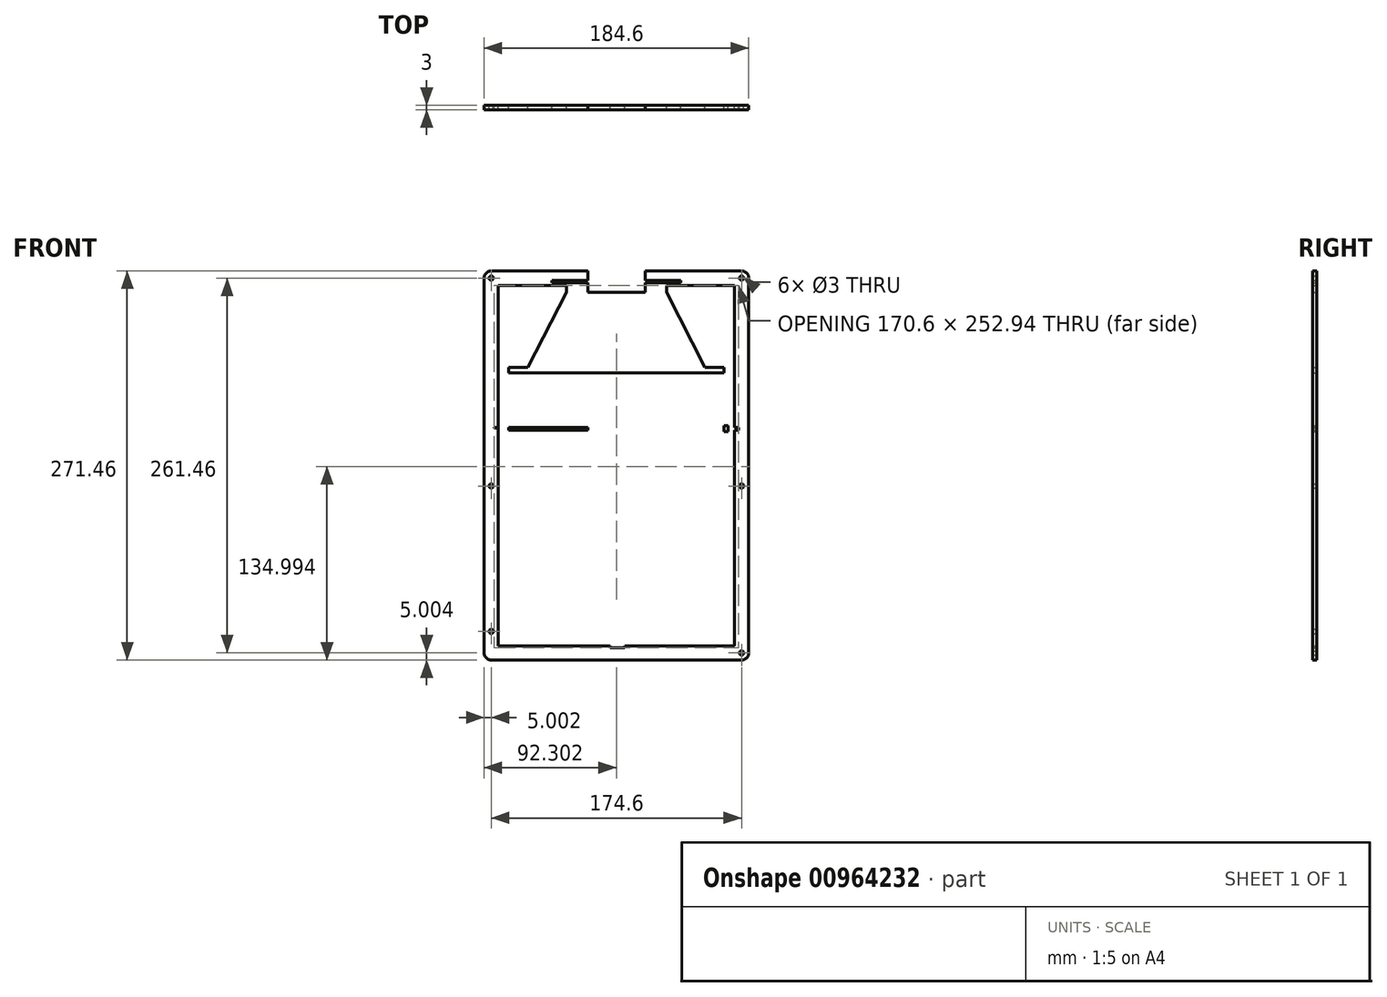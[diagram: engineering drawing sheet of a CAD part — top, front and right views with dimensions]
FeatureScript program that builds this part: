
annotation { "Feature Type Name" : "Feature", "Feature Type Description" : "" }
export const myFeature = defineFeature(function(context is Context, id is Id, definition is map)
    precondition{}
    {
        {
            var Q0;
            Q0=qCreatedBy(makeId("Front.planeOp"),FACE);
            var sketch = newSketch(context, id + "F0", { "sketchPlane" : qUnion([Q0])});
            skLineSegment(sketch, "E0.bottom", {"start": v(-91.77, 132.51) * mm, "end": v(82.83, 132.51) * mm});
            skLineSegment(sketch, "E0.top", {"start": v(-91.77, -138.95) * mm, "end": v(82.83, -138.95) * mm});
            skLineSegment(sketch, "E0.left", {"start": v(-96.77, 127.51) * mm, "end": v(-96.77, -133.95) * mm});
            skLineSegment(sketch, "E0.right", {"start": v(87.83, 127.51) * mm, "end": v(87.83, -133.95) * mm});
            skPoint(sketch, "E1.visualSharp", {"position": v(-96.77, 132.51) * mm});
            skArc(sketch, "E1.filletArc", {"start": v(-91.77, 132.51) * mm, "mid": v(-95.3, 131.05) * mm, "end": v(-96.77, 127.51) * mm});
            skPoint(sketch, "E2.visualSharp", {"position": v(87.83, 132.51) * mm});
            skArc(sketch, "E2.filletArc", {"start": v(87.83, 127.51) * mm, "mid": v(86.37, 131.05) * mm, "end": v(82.83, 132.51) * mm});
            skPoint(sketch, "E3.visualSharp", {"position": v(87.83, -138.95) * mm});
            skArc(sketch, "E3.filletArc", {"start": v(82.83, -138.95) * mm, "mid": v(86.37, -137.48) * mm, "end": v(87.83, -133.95) * mm});
            skPoint(sketch, "E4.visualSharp", {"position": v(-96.77, -138.95) * mm});
            skArc(sketch, "E4.filletArc", {"start": v(-96.77, -133.95) * mm, "mid": v(-95.3, -137.48) * mm, "end": v(-91.77, -138.95) * mm});
            skCircle(sketch, "E5", {"center": v(-91.77, 127.51) * mm, "radius": 1.5 * mm});
            skCircle(sketch, "E6", {"center": v(82.83, 127.51) * mm, "radius": 1.5 * mm});
            skCircle(sketch, "E7", {"center": v(82.83, -133.95) * mm, "radius": 1.5 * mm});
            skCircle(sketch, "E8", {"center": v(-91.77, -17.49) * mm, "radius": 1.5 * mm});
            skCircle(sketch, "E9", {"center": v(82.83, -17.49) * mm, "radius": 1.5 * mm});
            skLineSegment(sketch, "E10.bottom", {"start": v(-86.77, 122.51) * mm, "end": v(77.83, 122.51) * mm});
            skLineSegment(sketch, "E10.top", {"start": v(-86.77, -128.95) * mm, "end": v(77.83, -128.95) * mm});
            skLineSegment(sketch, "E10.left", {"start": v(-86.77, 122.51) * mm, "end": v(-86.77, -128.95) * mm});
            skLineSegment(sketch, "E10.right", {"start": v(77.83, 122.51) * mm, "end": v(77.83, -128.95) * mm});
            skLineSegment(sketch, "E11.bottom", {"start": v(-8.77, -128.95) * mm, "end": v(1.23, -128.95) * mm});
            skLineSegment(sketch, "E11.top", {"start": v(-8.77, -130.43) * mm, "end": v(1.23, -130.43) * mm});
            skLineSegment(sketch, "E11.left", {"start": v(-8.77, -128.95) * mm, "end": v(-8.77, -130.43) * mm});
            skLineSegment(sketch, "E11.right", {"start": v(1.23, -128.95) * mm, "end": v(1.23, -130.43) * mm});
            skLineSegment(sketch, "E12.bottom", {"start": v(-11.27, -130.43) * mm, "end": v(3.73, -130.43) * mm});
            skLineSegment(sketch, "E12.top", {"start": v(-11.27, -132.03) * mm, "end": v(3.73, -132.03) * mm});
            skLineSegment(sketch, "E12.left", {"start": v(-11.27, -130.43) * mm, "end": v(-11.27, -132.03) * mm});
            skLineSegment(sketch, "E12.right", {"start": v(3.73, -130.43) * mm, "end": v(3.73, -132.03) * mm});
            skLineSegment(sketch, "E13.bottom", {"start": v(-89.77, 23.45) * mm, "end": v(80.83, 23.45) * mm});
            skLineSegment(sketch, "E13.top", {"start": v(-89.77, 21.45) * mm, "end": v(80.83, 21.45) * mm});
            skLineSegment(sketch, "E13.left", {"start": v(-89.77, 23.45) * mm, "end": v(-89.77, 21.45) * mm});
            skLineSegment(sketch, "E13.right", {"start": v(80.83, 23.45) * mm, "end": v(80.83, 21.45) * mm});
            skLineSegment(sketch, "E14.bottom", {"start": v(-86.77, 23.45) * mm, "end": v(77.83, 23.45) * mm});
            skLineSegment(sketch, "E14.left", {"start": v(-86.77, 23.45) * mm, "end": v(-86.77, 24.64) * mm});
            skLineSegment(sketch, "E14.right", {"start": v(77.83, 23.45) * mm, "end": v(77.83, 24.64) * mm});
            skLineSegment(sketch, "E15.bottom", {"start": v(77.83, 21.45) * mm, "end": v(-86.77, 21.45) * mm});
            skLineSegment(sketch, "E15.top", {"start": v(77.83, 16.15) * mm, "end": v(-86.77, 16.15) * mm});
            skLineSegment(sketch, "E15.left", {"start": v(77.83, 21.45) * mm, "end": v(77.83, 16.15) * mm});
            skLineSegment(sketch, "E15.right", {"start": v(-86.77, 21.45) * mm, "end": v(-86.77, 16.15) * mm});
            skLineSegment(sketch, "E16.bottom", {"start": v(-39.47, 124.21) * mm, "end": v(30.53, 124.21) * mm});
            skLineSegment(sketch, "E16.top", {"start": v(-39.47, 122.51) * mm, "end": v(30.53, 122.51) * mm});
            skLineSegment(sketch, "E16.left", {"start": v(-39.47, 124.21) * mm, "end": v(-39.47, 122.51) * mm});
            skLineSegment(sketch, "E16.right", {"start": v(30.53, 124.21) * mm, "end": v(30.53, 122.51) * mm});
            skLineSegment(sketch, "E17.bottom", {"start": v(-49.47, 125.81) * mm, "end": v(40.53, 125.81) * mm});
            skLineSegment(sketch, "E17.top", {"start": v(-49.47, 124.21) * mm, "end": v(40.53, 124.21) * mm});
            skLineSegment(sketch, "E17.left", {"start": v(-49.47, 125.81) * mm, "end": v(-49.47, 124.21) * mm});
            skLineSegment(sketch, "E17.right", {"start": v(40.53, 125.81) * mm, "end": v(40.53, 124.21) * mm});
            skLineSegment(sketch, "E18.bottom", {"start": v(-24.47, 132.51) * mm, "end": v(15.53, 132.51) * mm});
            skLineSegment(sketch, "E18.top", {"start": v(-24.47, 125.81) * mm, "end": v(15.53, 125.81) * mm});
            skLineSegment(sketch, "E18.left", {"start": v(-24.47, 132.51) * mm, "end": v(-24.47, 125.81) * mm});
            skLineSegment(sketch, "E18.right", {"start": v(15.53, 132.51) * mm, "end": v(15.53, 125.81) * mm});
            skLineSegment(sketch, "E19.bottom", {"start": v(30.53, 124.21) * mm, "end": v(40.53, 124.21) * mm});
            skLineSegment(sketch, "E19.top", {"start": v(21.23, 125.81) * mm, "end": v(40.53, 125.81) * mm});
            skLineSegment(sketch, "E19.right", {"start": v(40.53, 124.21) * mm, "end": v(40.53, 125.81) * mm});
            skLineSegment(sketch, "E20.bottom", {"start": v(-39.47, 124.21) * mm, "end": v(-49.47, 124.21) * mm});
            skLineSegment(sketch, "E20.top", {"start": v(-28.77, 125.81) * mm, "end": v(-49.47, 125.81) * mm});
            skLineSegment(sketch, "E20.right", {"start": v(-49.47, 124.21) * mm, "end": v(-49.47, 125.81) * mm});
            skLineSegment(sketch, "E21.bottom", {"start": v(30.53, 122.51) * mm, "end": v(40.53, 122.51) * mm});
            skLineSegment(sketch, "E22.bottom", {"start": v(-39.47, 122.51) * mm, "end": v(-40.47, 122.51) * mm});
            skLineSegment(sketch, "E23.top", {"start": v(-86.77, -22.49) * mm, "end": v(-96.77, -22.49) * mm});
            skLineSegment(sketch, "E23.left", {"start": v(-86.77, -130.99) * mm, "end": v(-86.77, -22.49) * mm});
            skLineSegment(sketch, "E23.right", {"start": v(-96.77, -132.28) * mm, "end": v(-96.77, -22.49) * mm});
            skLineSegment(sketch, "E24.top", {"start": v(-39.47, 117.51) * mm, "end": v(30.53, 117.51) * mm});
            skLineSegment(sketch, "E24.left", {"start": v(-39.47, 122.51) * mm, "end": v(-39.47, 117.51) * mm});
            skLineSegment(sketch, "E24.right", {"start": v(30.53, 122.51) * mm, "end": v(30.53, 117.51) * mm});
            skLineSegment(sketch, "E25.bottom", {"start": v(-96.77, -113.95) * mm, "end": v(-86.77, -113.95) * mm});
            skLineSegment(sketch, "E25.top", {"start": v(-96.77, -128.95) * mm, "end": v(-86.77, -128.95) * mm});
            skLineSegment(sketch, "E25.left", {"start": v(-96.77, -113.95) * mm, "end": v(-96.77, -128.95) * mm});
            skLineSegment(sketch, "E25.right", {"start": v(-86.77, -113.95) * mm, "end": v(-86.77, -128.95) * mm});
            skCircle(sketch, "E26", {"center": v(-91.77, -118.95) * mm, "radius": 1.5 * mm});
            skLineSegment(sketch, "E27", {"start": v(-39.47, 117.51) * mm, "end": v(-86.77, 24.64) * mm});
            skLineSegment(sketch, "E28", {"start": v(30.53, 117.51) * mm, "end": v(77.83, 24.64) * mm});
            skLineSegment(sketch, "E29.bottom", {"start": v(-89.77, 23.45) * mm, "end": v(-86.77, 23.45) * mm});
            skLineSegment(sketch, "E29.left", {"start": v(-89.77, 23.45) * mm, "end": v(-89.77, 22.05) * mm});
            skCircle(sketch, "E30", {"center": v(-63.77, 79.64) * mm, "radius": 1.5 * mm});
            skCircle(sketch, "E31", {"center": v(54.83, 79.64) * mm, "radius": 1.5 * mm});
            skLineSegment(sketch, "E32.top", {"start": v(-86.77, 53.45) * mm, "end": v(77.83, 53.45) * mm});
            skLineSegment(sketch, "E32.left", {"start": v(-86.77, 23.45) * mm, "end": v(-86.77, 53.45) * mm});
            skLineSegment(sketch, "E32.right", {"start": v(77.83, 23.45) * mm, "end": v(77.83, 53.45) * mm});
            skLineSegment(sketch, "E33.bottom", {"start": v(80.83, 21.45) * mm, "end": v(77.83, 21.45) * mm});
            skLineSegment(sketch, "E33.top", {"start": v(80.83, 22.85) * mm, "end": v(77.83, 22.85) * mm});
            skLineSegment(sketch, "E33.left", {"start": v(80.83, 21.45) * mm, "end": v(80.83, 22.85) * mm});
            skLineSegment(sketch, "E33.right", {"start": v(77.83, 21.45) * mm, "end": v(77.83, 22.85) * mm});
            skLineSegment(sketch, "E34.bottom", {"start": v(-89.77, 22.85) * mm, "end": v(-86.77, 22.85) * mm});
            skLineSegment(sketch, "E34.top", {"start": v(-89.77, 21.45) * mm, "end": v(-86.77, 21.45) * mm});
            skLineSegment(sketch, "E34.left", {"start": v(-89.77, 22.85) * mm, "end": v(-89.77, 21.45) * mm});
            skLineSegment(sketch, "E34.right", {"start": v(-86.77, 22.85) * mm, "end": v(-86.77, 21.45) * mm});
            skLineSegment(sketch, "E35.bottom", {"start": v(77.83, 23.45) * mm, "end": v(-76.6, 23.45) * mm});
            skLineSegment(sketch, "E36.bottom", {"start": v(-86.77, 56.45) * mm, "end": v(77.83, 56.45) * mm});
            skLineSegment(sketch, "E36.right", {"start": v(77.83, 56.45) * mm, "end": v(77.83, 20.45) * mm});
            skLineSegment(sketch, "E37.top", {"start": v(-24.47, 12.51) * mm, "end": v(15.53, 12.51) * mm});
            skLineSegment(sketch, "E37.left", {"start": v(-24.47, 125.81) * mm, "end": v(-24.47, 12.51) * mm});
            skLineSegment(sketch, "E37.right", {"start": v(15.53, 125.81) * mm, "end": v(15.53, 12.51) * mm});
            skLineSegment(sketch, "E38.bottom", {"start": v(77.83, 23.45) * mm, "end": v(-86.77, 23.45) * mm});
            skLineSegment(sketch, "E38.top", {"start": v(77.83, 24.45) * mm, "end": v(-86.77, 24.45) * mm});
            skLineSegment(sketch, "E38.left", {"start": v(77.83, 23.45) * mm, "end": v(77.83, 24.45) * mm});
            skLineSegment(sketch, "E38.right", {"start": v(-86.77, 23.45) * mm, "end": v(-86.77, 24.45) * mm});
            skLineSegment(sketch, "E39.bottom", {"start": v(70.53, 65.1) * mm, "end": v(-79.47, 65.1) * mm});
            skLineSegment(sketch, "E39.top", {"start": v(70.53, 24.45) * mm, "end": v(-79.47, 24.45) * mm});
            skLineSegment(sketch, "E39.left", {"start": v(70.53, 65.1) * mm, "end": v(70.53, 24.45) * mm});
            skLineSegment(sketch, "E39.right", {"start": v(-79.47, 65.1) * mm, "end": v(-79.47, 24.45) * mm});
            skLineSegment(sketch, "E40.bottom", {"start": v(77.83, 20.45) * mm, "end": v(-86.77, 20.45) * mm});
            skLineSegment(sketch, "E40.left", {"start": v(77.83, 20.45) * mm, "end": v(77.83, 4.5) * mm});
            skLineSegment(sketch, "E40.right", {"start": v(-86.77, 20.45) * mm, "end": v(-86.77, 0) * mm});
            skLineSegment(sketch, "E41.bottom", {"start": v(77.83, 20.45) * mm, "end": v(70.53, 20.45) * mm});
            skLineSegment(sketch, "E41.top", {"start": v(77.83, 24.45) * mm, "end": v(70.53, 24.45) * mm});
            skLineSegment(sketch, "E41.left", {"start": v(77.83, 20.45) * mm, "end": v(77.83, 24.45) * mm});
            skLineSegment(sketch, "E41.right", {"start": v(70.53, 20.45) * mm, "end": v(70.53, 24.45) * mm});
            skLineSegment(sketch, "E42.bottom", {"start": v(-86.77, 21.45) * mm, "end": v(-79.47, 21.45) * mm});
            skLineSegment(sketch, "E42.top", {"start": v(-86.77, 24.45) * mm, "end": v(-79.47, 24.45) * mm});
            skLineSegment(sketch, "E42.left", {"start": v(-86.77, 21.45) * mm, "end": v(-86.77, 24.45) * mm});
            skLineSegment(sketch, "E43.bottom", {"start": v(-79.47, 24.45) * mm, "end": v(-86.77, 24.45) * mm});
            skLineSegment(sketch, "E43.top", {"start": v(-79.47, 20.45) * mm, "end": v(-86.77, 20.45) * mm});
            skLineSegment(sketch, "E43.left", {"start": v(-79.47, 24.45) * mm, "end": v(-79.47, 20.45) * mm});
            skLineSegment(sketch, "E43.right", {"start": v(-86.77, 24.45) * mm, "end": v(-86.77, 20.45) * mm});
            skLineSegment(sketch, "E44.bottom", {"start": v(-79.47, 56.45) * mm, "end": v(-82.47, 56.45) * mm});
            skLineSegment(sketch, "E44.top", {"start": v(-79.47, 20.45) * mm, "end": v(-82.47, 20.45) * mm});
            skLineSegment(sketch, "E44.left", {"start": v(-79.47, 56.45) * mm, "end": v(-79.47, 20.45) * mm});
            skLineSegment(sketch, "E44.right", {"start": v(-82.47, 56.45) * mm, "end": v(-82.47, 20.45) * mm});
            skLineSegment(sketch, "E45.bottom", {"start": v(70.53, 56.45) * mm, "end": v(73.53, 56.45) * mm});
            skLineSegment(sketch, "E45.top", {"start": v(70.53, 20.45) * mm, "end": v(73.53, 20.45) * mm});
            skLineSegment(sketch, "E45.left", {"start": v(70.53, 56.45) * mm, "end": v(70.53, 20.45) * mm});
            skLineSegment(sketch, "E45.right", {"start": v(73.53, 56.45) * mm, "end": v(73.53, 20.45) * mm});
            skLineSegment(sketch, "E46.bottom", {"start": v(-86.77, 60.75) * mm, "end": v(77.83, 60.75) * mm});
            skLineSegment(sketch, "E46.top", {"start": v(-86.77, -1.52) * mm, "end": v(77.83, -1.52) * mm});
            skLineSegment(sketch, "E46.left", {"start": v(-86.77, 60.75) * mm, "end": v(-86.77, -1.52) * mm});
            skLineSegment(sketch, "E46.right", {"start": v(77.83, 60.75) * mm, "end": v(77.83, -1.52) * mm});
            skLineSegment(sketch, "E47.bottom", {"start": v(77.83, 56.45) * mm, "end": v(-86.77, 56.45) * mm});
            skLineSegment(sketch, "E47.top", {"start": v(77.83, 61.45) * mm, "end": v(-86.77, 61.45) * mm});
            skLineSegment(sketch, "E47.left", {"start": v(77.83, 56.45) * mm, "end": v(77.83, 61.45) * mm});
            skLineSegment(sketch, "E47.right", {"start": v(-86.77, 56.45) * mm, "end": v(-86.77, 61.45) * mm});
            skSolve(sketch);
        }
        {
            var Q0;
            {var subQ0=sQuery(id+"F0.wireOp",EDGE,"E15.left");Q0=makeQuery(id+"F0.imprint","IMPRINT",FACE,{"disambiguationData":[TD([[makeQuery(id+"F0.imprint","IMPRINT",EDGE,{"derivedFrom":subQ0}),-1.0]])]});}
            var Q1;
            {var subQ5=sQuery(id+"F0.wireOp",EDGE,"E35.left");Q1=makeQuery(id+"F0.imprint","IMPRINT",FACE,{"disambiguationData":[TD([[makeQuery(id+"F0.imprint","IMPRINT",EDGE,{"derivedFrom":subQ5}),1.0]])]});}
            var Q2;
            {var subQ0=sQuery(id+"F0.wireOp",EDGE,"E37.right");var subQ1=sQuery(id+"F0.wireOp",EDGE,"E35.top");var subQ2=makeQuery(id+"F0.imprint","INTERSECT",VERTEX,{"derivedFrom":[subQ1,subQ0]});Q2=makeQuery(id+"F0.imprint","IMPRINT",FACE,{"disambiguationData":[TD([[makeQuery(id+"F0.imprint","IMPRINT",EDGE,{"disambiguationData":[TD([[subQ2,-1.0]])],"derivedFrom":subQ1}),1.0]])]});}
            var Q3;
            {var subQ5=sQuery(id+"F0.wireOp",EDGE,"E35.right");Q3=makeQuery(id+"F0.imprint","IMPRINT",FACE,{"disambiguationData":[TD([[makeQuery(id+"F0.imprint","IMPRINT",EDGE,{"derivedFrom":subQ5}),-1.0]])]});}
            var Q4;
            {var subQ0=sQuery(id+"F0.wireOp",EDGE,"E22.bottom");Q4=makeQuery(id+"F0.imprint","IMPRINT",FACE,{"disambiguationData":[TD([[makeQuery(id+"F0.imprint","IMPRINT",EDGE,{"derivedFrom":subQ0}),1.0]])]});}
            var Q5;
            {var subQ0=sQuery(id+"F0.wireOp",EDGE,"E27");var subQ5=sQuery(id+"F0.wireOp",EDGE,"E35.top");var subQ6=makeQuery(id+"F0.imprint","INTERSECT",VERTEX,{"derivedFrom":[subQ0,subQ5]});Q5=makeQuery(id+"F0.imprint","IMPRINT",FACE,{"disambiguationData":[TD([[makeQuery(id+"F0.imprint","IMPRINT",EDGE,{"disambiguationData":[TD([[subQ6,1.0]])],"derivedFrom":subQ5}),-1.0]])]});}
            var Q6;
            {var subQ0=sQuery(id+"F0.wireOp",EDGE,"E28");var subQ5=sQuery(id+"F0.wireOp",EDGE,"E35.top");var subQ6=makeQuery(id+"F0.imprint","INTERSECT",VERTEX,{"derivedFrom":[subQ0,subQ5]});Q6=makeQuery(id+"F0.imprint","IMPRINT",FACE,{"disambiguationData":[TD([[makeQuery(id+"F0.imprint","IMPRINT",EDGE,{"disambiguationData":[TD([[subQ6,-1.0]])],"derivedFrom":subQ5}),-1.0]])]});}
            var Q7;
            {var subQ0=sQuery(id+"F0.wireOp",EDGE,"E21.bottom");Q7=makeQuery(id+"F0.imprint","IMPRINT",FACE,{"disambiguationData":[TD([[makeQuery(id+"F0.imprint","IMPRINT",EDGE,{"derivedFrom":subQ0}),-1.0]])]});}
            var Q8;
            Q8=makeQuery(id+"F0.imprint","IMPRINT",FACE,{"disambiguationData":[TD([[makeQuery(id+"F0.imprint","IMPRINT",EDGE,{"derivedFrom":sQuery(id+"F0.wireOp",EDGE,"E25.bottom")}),-1.0]])]});
            var Q9;
            {var subQ3=sQuery(id+"F0.wireOp",EDGE,"E1.filletArc");Q9=makeQuery(id+"F0.imprint","IMPRINT",FACE,{"disambiguationData":[TD([[makeQuery(id+"F0.imprint","IMPRINT",EDGE,{"derivedFrom":subQ3}),1.0]])]});}
            var Q10;
            Q10=makeQuery(id+"F0.imprint","IMPRINT",FACE,{"disambiguationData":[TD([[makeQuery(id+"F0.imprint","IMPRINT",EDGE,{"derivedFrom":sQuery(id+"F0.wireOp",EDGE,"E0.top")}),1.0]])]});
            var Q11;
            {var subQ5=sQuery(id+"F0.wireOp",EDGE,"E38.right");Q11=makeQuery(id+"F0.imprint","IMPRINT",FACE,{"disambiguationData":[TD([[makeQuery(id+"F0.imprint","IMPRINT",EDGE,{"derivedFrom":subQ5}),-1.0]])]});}
            var Q12;
            {var subQ5=sQuery(id+"F0.wireOp",EDGE,"E38.left");Q12=makeQuery(id+"F0.imprint","IMPRINT",FACE,{"disambiguationData":[TD([[makeQuery(id+"F0.imprint","IMPRINT",EDGE,{"derivedFrom":subQ5}),1.0]])]});}
            var Q13;
            {var subQ1=sQuery(id+"F0.wireOp",EDGE,"E24.top");var subQ3=sQuery(id+"F0.wireOp",EDGE,"E37.left");var subQ4=makeQuery(id+"F0.imprint","INTERSECT",VERTEX,{"derivedFrom":[subQ1,subQ3]});Q13=makeQuery(id+"F0.imprint","IMPRINT",FACE,{"disambiguationData":[TD([[makeQuery(id+"F0.imprint","IMPRINT",EDGE,{"disambiguationData":[TD([[subQ4,-1.0]])],"derivedFrom":subQ3}),-1.0]])]});}
            var Q14;
            {var subQ0=sQuery(id+"F0.wireOp",EDGE,"E37.left");var subQ1=sQuery(id+"F0.wireOp",EDGE,"E24.top");var subQ2=makeQuery(id+"F0.imprint","INTERSECT",VERTEX,{"derivedFrom":[subQ1,subQ0]});Q14=makeQuery(id+"F0.imprint","IMPRINT",FACE,{"disambiguationData":[TD([[makeQuery(id+"F0.imprint","IMPRINT",EDGE,{"disambiguationData":[TD([[subQ2,-1.0]])],"derivedFrom":subQ1}),-1.0]])]});}
            var Q15;
            {var subQ1=sQuery(id+"F0.wireOp",EDGE,"E24.top");var subQ3=sQuery(id+"F0.wireOp",EDGE,"E37.right");var subQ4=makeQuery(id+"F0.imprint","INTERSECT",VERTEX,{"derivedFrom":[subQ1,subQ3]});Q15=makeQuery(id+"F0.imprint","IMPRINT",FACE,{"disambiguationData":[TD([[makeQuery(id+"F0.imprint","IMPRINT",EDGE,{"disambiguationData":[TD([[subQ4,-1.0]])],"derivedFrom":subQ3}),1.0]])]});}
            var Q16;
            {var subQ0=sQuery(id+"F0.wireOp",EDGE,"E39.bottom");var subQ1=sQuery(id+"F0.wireOp",EDGE,"E27");var subQ2=makeQuery(id+"F0.imprint","INTERSECT",VERTEX,{"derivedFrom":[subQ1,subQ0]});Q16=makeQuery(id+"F0.imprint","IMPRINT",FACE,{"disambiguationData":[TD([[makeQuery(id+"F0.imprint","IMPRINT",EDGE,{"disambiguationData":[TD([[subQ2,-1.0]])],"derivedFrom":subQ1}),-1.0]])]});}
            var Q17;
            {var subQ0=sQuery(id+"F0.wireOp",EDGE,"E39.bottom");var subQ1=sQuery(id+"F0.wireOp",EDGE,"E27");var subQ2=makeQuery(id+"F0.imprint","INTERSECT",VERTEX,{"derivedFrom":[subQ1,subQ0]});Q17=makeQuery(id+"F0.imprint","IMPRINT",FACE,{"disambiguationData":[TD([[makeQuery(id+"F0.imprint","IMPRINT",EDGE,{"disambiguationData":[TD([[subQ2,-1.0]])],"derivedFrom":subQ1}),1.0]])]});}
            var Q18;
            {var subQ0=sQuery(id+"F0.wireOp",EDGE,"E39.bottom");var subQ1=sQuery(id+"F0.wireOp",EDGE,"E28");var subQ2=makeQuery(id+"F0.imprint","INTERSECT",VERTEX,{"derivedFrom":[subQ1,subQ0]});Q18=makeQuery(id+"F0.imprint","IMPRINT",FACE,{"disambiguationData":[TD([[makeQuery(id+"F0.imprint","IMPRINT",EDGE,{"disambiguationData":[TD([[subQ2,-1.0]])],"derivedFrom":subQ1}),-1.0]])]});}
            var Q19;
            {var subQ0=sQuery(id+"F0.wireOp",EDGE,"E39.bottom");var subQ1=sQuery(id+"F0.wireOp",EDGE,"E28");var subQ2=makeQuery(id+"F0.imprint","INTERSECT",VERTEX,{"derivedFrom":[subQ1,subQ0]});Q19=makeQuery(id+"F0.imprint","IMPRINT",FACE,{"disambiguationData":[TD([[makeQuery(id+"F0.imprint","IMPRINT",EDGE,{"disambiguationData":[TD([[subQ2,-1.0]])],"derivedFrom":subQ1}),1.0]])]});}
            var Q20;
            {var subQ4=sQuery(id+"F0.wireOp",EDGE,"E41.right");var subQ6=sQuery(id+"F0.wireOp",EDGE,"E15.bottom");var subQ8=makeQuery(id+"F0.imprint","INTERSECT",VERTEX,{"derivedFrom":[subQ6,subQ4]});Q20=makeQuery(id+"F0.imprint","IMPRINT",FACE,{"disambiguationData":[TD([[makeQuery(id+"F0.imprint","IMPRINT",EDGE,{"disambiguationData":[TD([[subQ8,-1.0]])],"derivedFrom":subQ4}),-1.0]])]});}
            var Q21;
            {var subQ5=sQuery(id+"F0.wireOp",EDGE,"E42.top");Q21=makeQuery(id+"F0.imprint","IMPRINT",FACE,{"disambiguationData":[TD([[makeQuery(id+"F0.imprint","IMPRINT",EDGE,{"derivedFrom":subQ5}),-1.0]])]});}
            var Q22;
            {var subQ1=sQuery(id+"F0.wireOp",EDGE,"E24.top");var subQ3=sQuery(id+"F0.wireOp",EDGE,"E37.left");var subQ4=makeQuery(id+"F0.imprint","INTERSECT",VERTEX,{"derivedFrom":[subQ1,subQ3]});Q22=makeQuery(id+"F0.imprint","IMPRINT",FACE,{"disambiguationData":[TD([[makeQuery(id+"F0.imprint","IMPRINT",EDGE,{"disambiguationData":[TD([[subQ4,-1.0]])],"derivedFrom":subQ3}),-1.0]])]});}
            var Q23;
            {var subQ0=sQuery(id+"F0.wireOp",EDGE,"E39.bottom");var subQ1=sQuery(id+"F0.wireOp",EDGE,"E27");var subQ2=makeQuery(id+"F0.imprint","INTERSECT",VERTEX,{"derivedFrom":[subQ1,subQ0]});Q23=makeQuery(id+"F0.imprint","IMPRINT",FACE,{"disambiguationData":[TD([[makeQuery(id+"F0.imprint","IMPRINT",EDGE,{"disambiguationData":[TD([[subQ2,-1.0]])],"derivedFrom":subQ1}),1.0]])]});}
            var Q24;
            {var subQ0=sQuery(id+"F0.wireOp",EDGE,"E39.bottom");var subQ1=sQuery(id+"F0.wireOp",EDGE,"E37.left");var subQ2=makeQuery(id+"F0.imprint","INTERSECT",VERTEX,{"derivedFrom":[subQ1,subQ0]});Q24=makeQuery(id+"F0.imprint","IMPRINT",FACE,{"disambiguationData":[TD([[makeQuery(id+"F0.imprint","IMPRINT",EDGE,{"disambiguationData":[TD([[subQ2,-1.0]])],"derivedFrom":subQ1}),1.0]])]});}
            var Q25;
            {var subQ1=sQuery(id+"F0.wireOp",EDGE,"E24.top");var subQ3=sQuery(id+"F0.wireOp",EDGE,"E37.right");var subQ4=makeQuery(id+"F0.imprint","INTERSECT",VERTEX,{"derivedFrom":[subQ1,subQ3]});Q25=makeQuery(id+"F0.imprint","IMPRINT",FACE,{"disambiguationData":[TD([[makeQuery(id+"F0.imprint","IMPRINT",EDGE,{"disambiguationData":[TD([[subQ4,-1.0]])],"derivedFrom":subQ3}),1.0]])]});}
            var Q26;
            {var subQ0=sQuery(id+"F0.wireOp",EDGE,"E39.bottom");var subQ1=sQuery(id+"F0.wireOp",EDGE,"E28");var subQ2=makeQuery(id+"F0.imprint","INTERSECT",VERTEX,{"derivedFrom":[subQ1,subQ0]});Q26=makeQuery(id+"F0.imprint","IMPRINT",FACE,{"disambiguationData":[TD([[makeQuery(id+"F0.imprint","IMPRINT",EDGE,{"disambiguationData":[TD([[subQ2,-1.0]])],"derivedFrom":subQ1}),-1.0]])]});}
            var Q27;
            {var subQ0=sQuery(id+"F0.wireOp",EDGE,"E33.bottom");Q27=makeQuery(id+"F0.imprint","IMPRINT",FACE,{"disambiguationData":[TD([[makeQuery(id+"F0.imprint","IMPRINT",EDGE,{"derivedFrom":subQ0}),-1.0]])]});}
            var Q28;
            {var subQ0=sQuery(id+"F0.wireOp",EDGE,"E13.bottom");Q28=makeQuery(id+"F0.imprint","IMPRINT",FACE,{"disambiguationData":[TD([[makeQuery(id+"F0.imprint","IMPRINT",EDGE,{"derivedFrom":subQ0}),-1.0]])]});}
            var Q29;
            {var subQ8=sQuery(id+"F0.wireOp",EDGE,"E11.bottom");Q29=makeQuery(id+"F0.imprint","IMPRINT",FACE,{"disambiguationData":[TD([[makeQuery(id+"F0.imprint","IMPRINT",EDGE,{"derivedFrom":subQ8}),1.0]])]});}
            var Q30;
            {var subQ0=sQuery(id+"F0.wireOp",EDGE,"E23.top");Q30=makeQuery(id+"F0.imprint","IMPRINT",FACE,{"disambiguationData":[TD([[makeQuery(id+"F0.imprint","IMPRINT",EDGE,{"derivedFrom":subQ0}),1.0]])]});}
            var Q31;
            {var subQ3=sQuery(id+"F0.wireOp",EDGE,"E34.bottom");Q31=makeQuery(id+"F0.imprint","IMPRINT",FACE,{"disambiguationData":[TD([[makeQuery(id+"F0.imprint","IMPRINT",EDGE,{"derivedFrom":subQ3}),-1.0]])]});}
            var Q32;
            {var subQ0=sQuery(id+"F0.wireOp",EDGE,"E29.bottom");Q32=makeQuery(id+"F0.imprint","IMPRINT",FACE,{"disambiguationData":[TD([[makeQuery(id+"F0.imprint","IMPRINT",EDGE,{"derivedFrom":subQ0}),-1.0]])]});}
            var Q33;
            Q33=makeQuery(id+"F0.imprint","IMPRINT",FACE,{"disambiguationData":[TD([[makeQuery(id+"F0.imprint","IMPRINT",EDGE,{"derivedFrom":sQuery(id+"F0.wireOp",EDGE,"E18.bottom")}),-1.0]])]});
            var Q34;
            {var subQ5=sQuery(id+"F0.wireOp",EDGE,"E18.top");Q34=makeQuery(id+"F0.imprint","IMPRINT",FACE,{"disambiguationData":[TD([[makeQuery(id+"F0.imprint","IMPRINT",EDGE,{"derivedFrom":subQ5}),-1.0]])]});}
            var Q35;
            {var subQ0=sQuery(id+"F0.wireOp",EDGE,"E20.bottom");Q35=makeQuery(id+"F0.imprint","IMPRINT",FACE,{"disambiguationData":[TD([[makeQuery(id+"F0.imprint","IMPRINT",EDGE,{"derivedFrom":subQ0}),-1.0]])]});}
            var Q36;
            {var subQ0=sQuery(id+"F0.wireOp",EDGE,"E16.left");Q36=makeQuery(id+"F0.imprint","IMPRINT",FACE,{"disambiguationData":[TD([[makeQuery(id+"F0.imprint","IMPRINT",EDGE,{"derivedFrom":subQ0}),1.0]])]});}
            var Q37;
            {var subQ0=sQuery(id+"F0.wireOp",EDGE,"E24.left");Q37=makeQuery(id+"F0.imprint","IMPRINT",FACE,{"disambiguationData":[TD([[makeQuery(id+"F0.imprint","IMPRINT",EDGE,{"derivedFrom":subQ0}),1.0]])]});}
            var Q38;
            {var subQ0=sQuery(id+"F0.wireOp",EDGE,"E37.left");var subQ1=sQuery(id+"F0.wireOp",EDGE,"E16.top");var subQ2=makeQuery(id+"F0.imprint","INTERSECT",VERTEX,{"derivedFrom":[subQ1,subQ0]});Q38=makeQuery(id+"F0.imprint","IMPRINT",FACE,{"disambiguationData":[TD([[makeQuery(id+"F0.imprint","IMPRINT",EDGE,{"disambiguationData":[TD([[subQ2,-1.0]])],"derivedFrom":subQ1}),-1.0]])]});}
            var Q39;
            {var subQ0=sQuery(id+"F0.wireOp",EDGE,"E37.left");var subQ1=sQuery(id+"F0.wireOp",EDGE,"E17.top");var subQ2=makeQuery(id+"F0.imprint","INTERSECT",VERTEX,{"derivedFrom":[subQ1,subQ0]});Q39=makeQuery(id+"F0.imprint","IMPRINT",FACE,{"disambiguationData":[TD([[makeQuery(id+"F0.imprint","IMPRINT",EDGE,{"disambiguationData":[TD([[subQ2,-1.0]])],"derivedFrom":subQ1}),-1.0]])]});}
            var Q40;
            {var subQ0=sQuery(id+"F0.wireOp",EDGE,"E24.right");Q40=makeQuery(id+"F0.imprint","IMPRINT",FACE,{"disambiguationData":[TD([[makeQuery(id+"F0.imprint","IMPRINT",EDGE,{"derivedFrom":subQ0}),-1.0]])]});}
            var Q41;
            {var subQ0=sQuery(id+"F0.wireOp",EDGE,"E16.right");Q41=makeQuery(id+"F0.imprint","IMPRINT",FACE,{"disambiguationData":[TD([[makeQuery(id+"F0.imprint","IMPRINT",EDGE,{"derivedFrom":subQ0}),-1.0]])]});}
            var Q42;
            {var subQ0=sQuery(id+"F0.wireOp",EDGE,"E19.bottom");Q42=makeQuery(id+"F0.imprint","IMPRINT",FACE,{"disambiguationData":[TD([[makeQuery(id+"F0.imprint","IMPRINT",EDGE,{"derivedFrom":subQ0}),1.0]])]});}
            var Q43;
            Q43=makeQuery(id+"F0.imprint","IMPRINT",FACE,{"disambiguationData":[TD([[makeQuery(id+"F0.imprint","IMPRINT",EDGE,{"derivedFrom":sQuery(id+"F0.wireOp",EDGE,"E12.top")}),1.0]])]});
            var Q44;
            Q44=makeQuery(id+"F0.imprint","IMPRINT",FACE,{"disambiguationData":[TD([[makeQuery(id+"F0.imprint","IMPRINT",EDGE,{"derivedFrom":sQuery(id+"F0.wireOp",EDGE,"E11.bottom")}),-1.0]])]});
            extrude(context, id + "F1", {"entities" : qUnion([Q0, Q1, Q2, Q3, Q4, Q5, Q6, Q7, Q8, Q9, Q10, Q11, Q12, Q13, Q14, Q15, Q16, Q17, Q18, Q19, Q20, Q21, Q22, Q23, Q24, Q25, Q26, Q27, Q28, Q29, Q30, Q31, Q32, Q33, Q34, Q35, Q36, Q37, Q38, Q39, Q40, Q41, Q42, Q43, Q44]), "depth" : 3 * mm, "offsetDistance" : 25 * mm});
        }
    });
